# Revit family: Bricks-Top
name_source: partatom
category: Detail Items
revit_build: Autodesk Revit Architecture 2012 (Build: 20110210_1515)
units: mm (PartAtom-declared; Revit-internal decimal feet)

## types (29) — shared parameters

## per-type parameters (varying)
| type | Height | Joint | Keynote | Length | Thickness |
| Standard - 3/8" Joint | 0' - 2 1/4" | 0' - 0 3/8" | 04 21 00.A1 | 0' - 7 5/8" | 0' - 3 5/8" |
| Standard - 1/2" Joint | 0' - 2 9/32" | 0' - 0 1/2" | 04 21 00.A2 | 0' - 7 5/8" | 0' - 3 5/8" |
| Engineer - 3/8" Joint | 0' - 2 13/16" | 0' - 0 3/8" | 04 21 00.A3 | 0' - 7 5/8" | 0' - 3 5/8" |
| Engineer - 1/2" Joint | 0' - 2 11/16" | 0' - 0 1/2" | 04 21 00.A4 | 0' - 7 1/2" | 0' - 3 1/2" |
| Economy - 3/8" Joint | 0' - 3 5/8" | 0' - 0 3/8" | 04 21 00.A5 | 0' - 7 5/8" | 0' - 3 5/8" |
| Economy - 1/2" Joint | 0' - 3 1/2" | 0' - 0 1/2" | 04 21 00.A6 | 0' - 7 1/2" | 0' - 3 1/2" |
| Double - 3/8" Joint | 0' - 4 31/32" | 0' - 0 3/8" | 04 21 00.A7 | 0' - 7 5/8" | 0' - 3 5/8" |
| Double - 1/2" Joint | 0' - 4 27/32" | 0' - 0 1/2" | 04 21 00.A8 | 0' - 7 1/2" | 0' - 3 1/2" |
| Roman - 3/8" Joint | 0' - 1 5/8" | 0' - 0 3/8" | 04 21 00.A9 | 0' - 11 5/8" | 0' - 3 5/8" |
| Roman - 1/2" Joint | 0' - 1 1/2" | 0' - 0 1/2" | 04 21 00.A10 | 0' - 11 1/2" | 0' - 3 1/2" |
| Norman - 3/8" Joint | 0' - 2 9/32" | 0' - 0 3/8" | 04 21 00.A11 | 0' - 11 5/8" | 0' - 3 5/8" |
| Norman - 1/2" Joint | 0' - 2 5/32" | 0' - 0 1/2" | 04 21 00.A12 | 0' - 11 1/2" | 0' - 3 1/2" |
| Norwegian - 3/8" Joint | 0' - 2 13/16" | 0' - 0 3/8" | 04 21 00.A13 | 0' - 11 5/8" | 0' - 3 5/8" |
| Norwegian - 1/2" Joint | 0' - 2 11/16" | 0' - 0 1/2" | 04 21 00.A14 | 0' - 11 1/2" | 0' - 3 1/2" |
| Utility - 3/8" Joint | 0' - 3 5/8" | 0' - 0 3/8" | 04 21 00.A15 | 0' - 11 5/8" | 0' - 3 5/8" |
| Utility - 1/2" Joint | 0' - 3 1/2" | 0' - 0 1/2" | 04 21 00.A16 | 0' - 11 1/2" | 0' - 3 1/2" |
| Triple - 3/8" Joint | 0' - 4 31/32" | 0' - 0 3/8" | 04 21 00.A17 | 0' - 11 5/8" | 0' - 3 5/8" |
| Triple - 1/2" Joint | 0' - 4 27/32" | 0' - 0 1/2" | 04 21 00.A18 | 0' - 11 1/2" | 0' - 3 1/2" |
| Scr Brick - 1/2" Joint | 0' - 2 5/32" | 0' - 0 1/2" | 04 21 00.A19 | 0' - 11 1/2" | 0' - 5 1/2" |
| Norwegian 6" w 3/8" Joint | 0' - 2 13/16" | 0' - 0 3/8" | 04 21 00.A20 | 0' - 11 5/8" | 0' - 5 5/8" |
| Norwegian 6" w 1/2" Joint | 0' - 2 11/16" | 0' - 0 1/2" | 04 21 00.A21 | 0' - 11 1/2" | 0' - 5 1/2" |
| Jumbo 6" w 3/8" Joint | 0' - 3 5/8" | 0' - 0 3/8" | 04 21 00.A22 | 0' - 11 5/8" | 0' - 5 5/8" |
| Jumbo 6" w 1/2" Joint | 0' - 3 1/2" | 0' - 0 1/2" | 04 21 00.A23 | 0' - 11 1/2" | 0' - 5 1/2" |
| Jumbo 8" w 3/8" Joint | 0' - 3 5/8" | 0' - 0 3/8" | 04 21 00.A24 | 0' - 11 5/8" | 0' - 7 5/8" |
| Jumbo 8" w 1/2" Joint | 0' - 3 1/2" | 0' - 0 1/2" | 04 21 00.A25 | 0' - 11 1/2" | 0' - 7 1/2" |
| Square 8" w 3/8" Joint | 0' - 7 5/8" | 0' - 0 3/8" | 04 21 00.A26 | 0' - 7 5/8" | 0' - 3 5/8" |
| Square 8" w 1/2" Joint | 0' - 7 1/2" | 0' - 0 1/2" | 04 21 00.A27 | 0' - 7 1/2" | 0' - 3 1/2" |
| Square 12" w 3/8" Joint | 0' - 11 5/8" | 0' - 0 3/8" | 04 21 00.A28 | 0' - 11 5/8" | 0' - 3 5/8" |
| Square 12" w 1/2" Joint | 0' - 11 1/2" | 0' - 0 1/2" | 04 21 00.A29 | 0' - 11 1/2" | 0' - 3 1/2" |

## geometry (parser evidence)
native form markers: Sweep x1
no freeform markers — native parametric forms only
